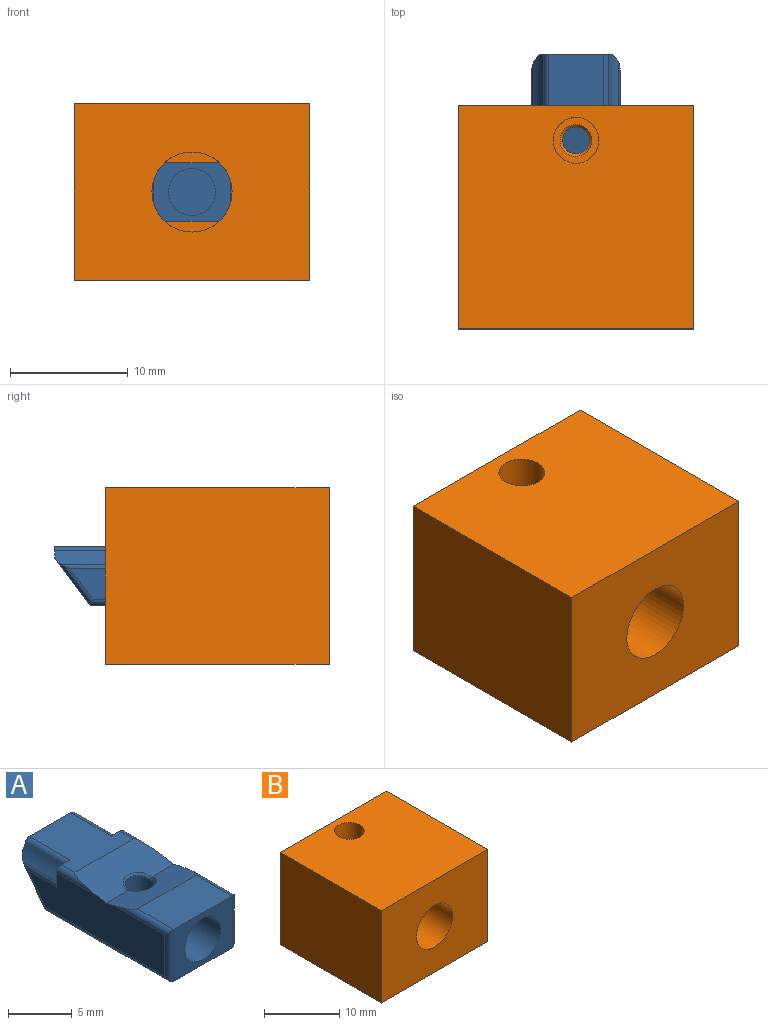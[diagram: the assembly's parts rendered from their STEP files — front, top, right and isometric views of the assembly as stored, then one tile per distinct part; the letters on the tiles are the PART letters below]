
ASSEMBLY  parts=2 mates=1
PART A: 33 faces, bbox 7.5x17x5 mm
  f0: plane 6.5x6mm, normal (0,0,1), area 30.4mm2, adj f2,f9,f13,f15,f27,f28,f29,f30
  f1: plane 15.2x4mm, normal (-1,0,0), area 53.6mm2, adj f8,f9,f15,f17,f18,f19,f20,f21
  f2: plane 6.26x1mm, normal (0,1,0), area 5.7mm2, adj f0,f12,f14,f16,f27,f28
  f3: plane 15.2x4mm, normal (1,0,0), area 53.6mm2, adj f8,f9,f13,f22,f23,f24,f25,f26
  f4: cylinder r=1.15mm len=4.41mm, axis (0,0,1), area 30.9mm2, adj f7,f10,f11
  f5: plane 6.5x5mm, normal (0,-1,0), area 19.9mm2, adj f6,f7,f18,f23,f31
  f6: plane 6.5x4mm, normal (0,0,1), area 26mm2, adj f5,f8,f17,f22
  f7: plane 14x6.5mm, normal (0,0,-1), area 86.8mm2, adj f4,f5,f16,f20,f24
  f8: plane 7.5x3mm, normal (0,0.23,0.97), area 19.8mm2, adj f1,f3,f6,f9,f11,f17,f22
  f9: plane 7.5x4mm, normal (0,-0.17,0.99), area 27mm2, adj f0,f1,f3,f8,f10,f29,f30
  f10: bspline ~2.7x1.35mm, area 1mm2, adj f4,f9,f11
  f11: bspline ~2.7x1.34mm, area 1mm2, adj f4,f8,f10
  f12: cylinder r=3.5mm len=4.5mm, axis (0,1,0), area 6.6mm2, adj f2,f13,f16,f25,f26,f27
  f13: plane 1.9x1.46mm, normal (0,1,0), area 1.1mm2, adj f0,f3,f12,f25,f27,f30
  f14: cylinder r=3.5mm len=4.5mm, axis (0,1,0), area 6.6mm2, adj f2,f15,f16,f19,f21,f28
  f15: plane 1.9x1.46mm, normal (0,1,0), area 1.1mm2, adj f0,f1,f14,f19,f28,f29
  f16: plane 6.5x4mm, normal (0,0.8,-0.6), area 32.5mm2, adj f2,f7,f12,f14,f21,f26
  f17: cylinder r=0.5mm len=6.14mm, axis (0,1,0), area 3.6mm2, adj f1,f6,f8,f18
  f18: cylinder r=0.5mm len=5mm, axis (0,0,-1), area 3.5mm2, adj f1,f5,f17,f20
  f19: cylinder r=0.5mm len=3.92mm, axis (0,1,0), area 1.4mm2, adj f1,f14,f15,f21
  f20: cylinder r=0.5mm len=14mm, axis (0,-1,0), area 10.7mm2, adj f1,f7,f18,f21
  f21: cylinder r=0.5mm len=4.14mm, axis (0,0.6,0.8), area 3.2mm2, adj f1,f14,f16,f19,f20
  f22: cylinder r=0.5mm len=6.14mm, axis (0,-1,0), area 3.6mm2, adj f3,f6,f8,f23
  f23: cylinder r=0.5mm len=5mm, axis (0,0,1), area 3.5mm2, adj f3,f5,f22,f24
  f24: cylinder r=0.5mm len=14mm, axis (0,1,0), area 10.7mm2, adj f3,f7,f23,f26
  f25: cylinder r=0.5mm len=3.92mm, axis (0,1,0), area 1.4mm2, adj f3,f12,f13,f26
  f26: cylinder r=0.5mm len=4.14mm, axis (0,0.6,0.8), area 3.2mm2, adj f3,f12,f16,f24,f25
  f27: cylinder r=0.5mm len=4.5mm, axis (0,1,0), area 2.7mm2, adj f0,f2,f12,f13
  f28: cylinder r=0.5mm len=4.5mm, axis (0,1,0), area 2.7mm2, adj f0,f2,f14,f15
  f29: cylinder r=0.5mm len=4.36mm, axis (0,1,0), area 2mm2, adj f0,f1,f9,f15
  f30: cylinder r=0.5mm len=4.36mm, axis (0,-1,0), area 2mm2, adj f0,f3,f9,f13
  f31: cylinder r=2mm len=4mm, axis (0,-1,0), area 37.7mm2, adj f5,f32
  f32: plane 4x4mm, normal (0,-1,0), area 12.6mm2, adj f31
PART B: 31 faces, bbox 20x19x15 mm
  f0: plane 20x19mm, normal (0,0,-1), area 350.9mm2, adj f7,f8,f10,f21,f22,f26,f28
  f1: plane 13x7.5mm, normal (0,0,-1), area 84.1mm2, adj f3,f4,f6,f7,f12,f13,f24,f25
  f2: plane 13x7.5mm, normal (0,0,1), area 82.6mm2, adj f3,f4,f7,f11,f12,f23,f24,f25
  f3: plane 13x5mm, normal (1,0,0), area 65mm2, adj f1,f2,f7,f25
  f4: plane 13x5mm, normal (-1,0,0), area 65mm2, adj f1,f2,f7,f24
  f5: cylinder r=1.15mm len=2.3mm, axis (0,0,-1), area 13mm2, adj f20,f23
  f6: cylinder r=1.15mm len=2.3mm, axis (0,0,1), area 13mm2, adj f1,f30
  f7: plane 20x15mm, normal (0,1,0), area 245.4mm2, adj f0,f1,f2,f3,f4,f8,f9,f10
  f8: plane 19x15mm, normal (1,0,0), area 285mm2, adj f0,f7,f9,f22
  f9: plane 20x19mm, normal (0,0,1), area 368.1mm2, adj f7,f8,f10,f19,f22
  f10: plane 19x15mm, normal (-1,0,0), area 285mm2, adj f0,f7,f9,f22
  f11: plane 4.61x0.9mm, normal (0,-1,0), area 2.8mm2, adj f2,f12
  f12: cylinder r=3.4mm len=8mm, axis (0,-1,0), area 148.4mm2, adj f1,f2,f11,f13,f22,f24,f25
  f13: plane 4.61x0.9mm, normal (0,-1,0), area 2.8mm2, adj f1,f12
  f14: cylinder r=1.65mm len=12mm, axis (0,1,0), area 124.4mm2, adj f7,f15
  f15: plane 3.3x3.3mm, normal (0,1,0), area 8.6mm2, adj f14
  f16: cylinder r=1.65mm len=12mm, axis (0,1,0), area 124.4mm2, adj f7,f17
  f17: plane 3.3x3.3mm, normal (0,1,0), area 8.6mm2, adj f16
  f18: plane 3.9x3.9mm, normal (0,0,1), area 6.2mm2, adj f19,f30
  f19: cylinder r=1.95mm len=3.9mm, axis (0,0,1), area 36.8mm2, adj f9,f18
  f20: plane 3.9x3.9mm, normal (0,0,-1), area 7.8mm2, adj f5,f21
  f21: cylinder r=1.95mm len=3.9mm, axis (0,0,-1), area 36.8mm2, adj f0,f20
  f22: plane 20x15mm, normal (0,-1,0), area 263.7mm2, adj f0,f8,f9,f10,f12
  f23: cone r=1.35mm half-angle=45deg, axis (0,0,1), area 2.2mm2, adj f2,f5
  f24: plane 5x1.45mm, normal (0,1,0), area 3.4mm2, adj f1,f2,f4,f12
  f25: plane 5x1.45mm, normal (0,1,0), area 3.4mm2, adj f1,f2,f3,f12
  f26: cylinder r=1.65mm len=10mm, axis (0,0,-1), area 103.7mm2, adj f0,f27
  f27: plane 3.3x3.3mm, normal (0,0,-1), area 8.6mm2, adj f26
  f28: cylinder r=1.65mm len=10mm, axis (0,0,-1), area 103.7mm2, adj f0,f29
  f29: plane 3.3x3.3mm, normal (0,0,-1), area 8.6mm2, adj f28
  f30: cone r=1.35mm half-angle=45deg, axis (0,0,1), area 2.2mm2, adj f6,f18
PLACE A t=(-7.43,4.96,0.04)mm
PLACE B t=(-7.43,5.69,0.04)mm fixed
MATE slider A.f31 <-> B.f12  axis (0,-1,0) through (-7.43,-2.04,2.54)mm
